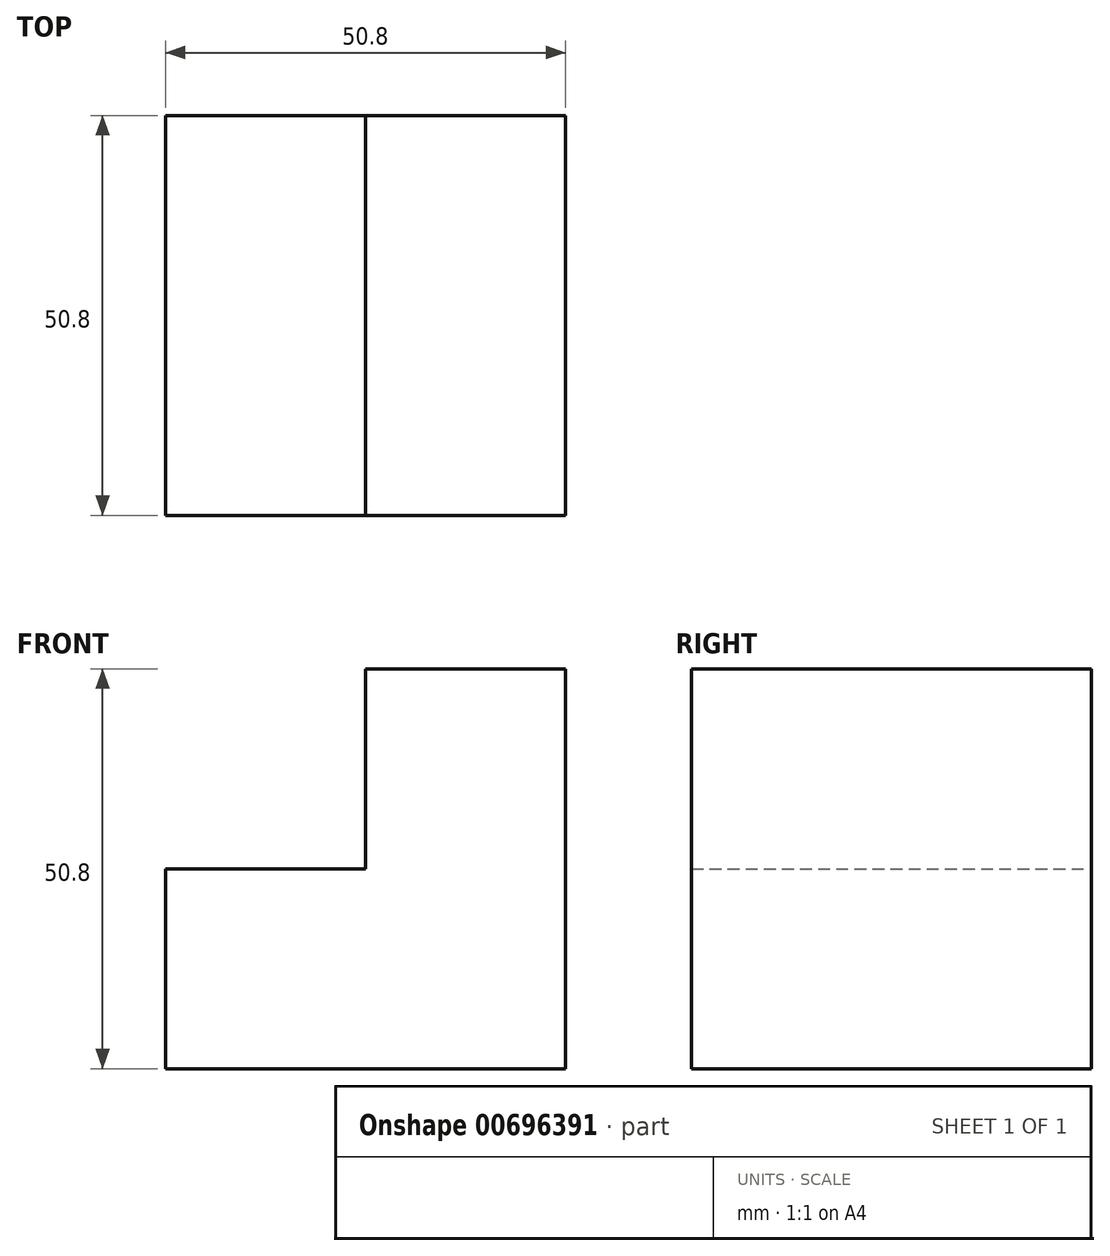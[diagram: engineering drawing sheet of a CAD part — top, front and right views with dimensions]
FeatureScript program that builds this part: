
annotation { "Feature Type Name" : "Feature", "Feature Type Description" : "" }
export const myFeature = defineFeature(function(context is Context, id is Id, definition is map)
    precondition{}
    {
        {
            var Q0;
            Q0=qCreatedBy(makeId("Front.planeOp"),FACE);
            var sketch = newSketch(context, id + "F0", { "sketchPlane" : qUnion([Q0])});
            skLineSegment(sketch, "E0.bottom", {"start": v(0, 0) * mm, "end": v(-50.8, 0) * mm});
            skLineSegment(sketch, "E0.top", {"start": v(0, 50.8) * mm, "end": v(-50.8, 50.8) * mm});
            skLineSegment(sketch, "E0.left", {"start": v(0, 0) * mm, "end": v(0, 50.8) * mm});
            skLineSegment(sketch, "E0.right", {"start": v(-50.8, 0) * mm, "end": v(-50.8, 50.8) * mm});
            skLineSegment(sketch, "E1.bottom", {"start": v(-50.8, 50.8) * mm, "end": v(-25.4, 50.8) * mm});
            skLineSegment(sketch, "E1.top", {"start": v(-50.8, 25.4) * mm, "end": v(-25.4, 25.4) * mm});
            skLineSegment(sketch, "E1.left", {"start": v(-50.8, 50.8) * mm, "end": v(-50.8, 25.4) * mm});
            skLineSegment(sketch, "E1.right", {"start": v(-25.4, 50.8) * mm, "end": v(-25.4, 25.4) * mm});
            skSolve(sketch);
        }
        {
            var Q0;
            Q0=makeQuery(id+"F0.imprint","IMPRINT",FACE,{"disambiguationData":[TD([[makeQuery(id+"F0.imprint","IMPRINT",EDGE,{"derivedFrom":sQuery(id+"F0.wireOp",EDGE,"E0.bottom")}),-1.0]])]});
            extrude(context, id + "F1", {"entities" : qUnion([Q0]), "depth" : 50.8 * mm, "offsetDistance" : 25.4 * mm});
        }
    });
